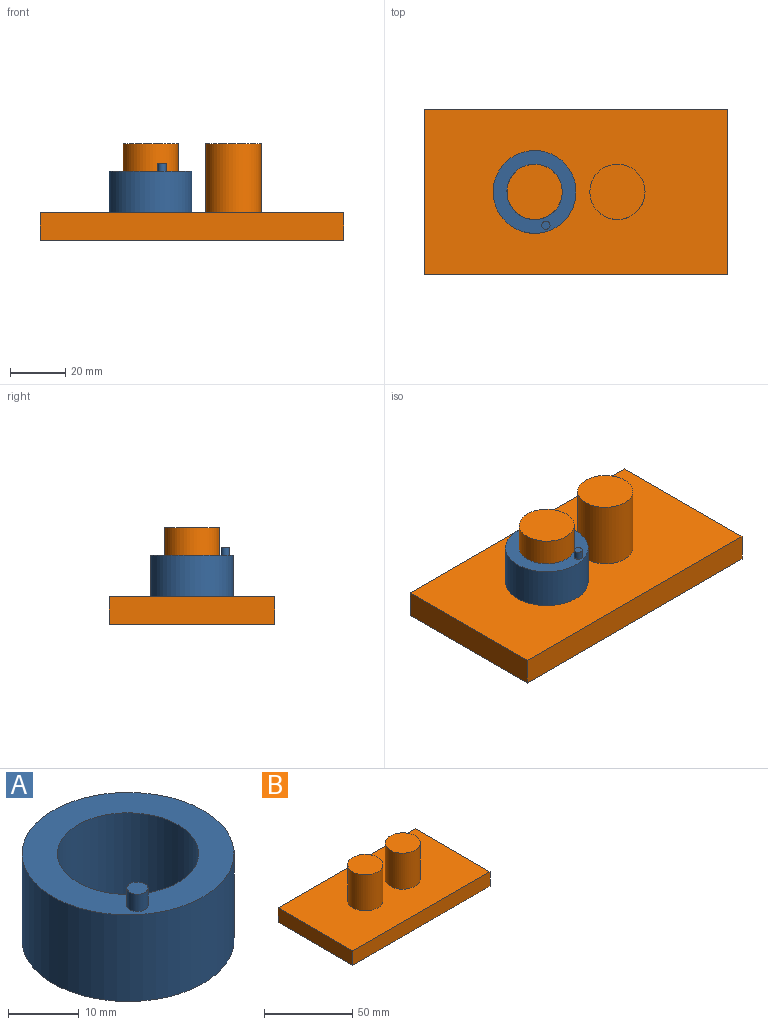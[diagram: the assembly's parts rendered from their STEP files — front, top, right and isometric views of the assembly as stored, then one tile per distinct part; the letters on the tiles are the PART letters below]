
ASSEMBLY  parts=2 mates=2
PART A: 6 faces, bbox 30x30x18 mm
  f0: cylinder r=10mm len=20mm, axis (0,0,-1), area 942.5mm2, adj f2,f3
  f1: cylinder r=15mm len=30mm, axis (0,0,-1), area 1413.7mm2, adj f2,f3
  f2: plane 30x30mm, normal (0,0,1), area 385.6mm2, adj f0,f1,f4
  f3: plane 30x30mm, normal (0,0,-1), area 392.7mm2, adj f0,f1
  f4: cylinder r=1.5mm len=3mm, axis (0,0,-1), area 28.3mm2, adj f2,f5
  f5: plane 3x3mm, normal (0,0,1), area 7.1mm2, adj f4
PART B: 10 faces, bbox 110x60x35 mm
  f0: plane 110x10mm, normal (0,1,0), area 1100mm2, adj f1,f3,f4,f5
  f1: plane 60x10mm, normal (-1,0,0), area 600mm2, adj f0,f2,f4,f5
  f2: plane 110x10mm, normal (0,-1,0), area 1100mm2, adj f1,f3,f4,f5
  f3: plane 60x10mm, normal (1,0,0), area 600mm2, adj f0,f2,f4,f5
  f4: plane 110x60mm, normal (0,0,1), area 5971.7mm2, adj f0,f1,f2,f3,f6,f8
  f5: plane 110x60mm, normal (0,0,-1), area 6600mm2, adj f0,f1,f2,f3
  f6: cylinder r=10mm len=25mm, axis (0,0,-1), area 1570.8mm2, adj f4,f7
  f7: plane 20x20mm, normal (0,0,1), area 314.2mm2, adj f6
  f8: cylinder r=10mm len=25mm, axis (0,0,-1), area 1570.8mm2, adj f4,f9
  f9: plane 20x20mm, normal (0,0,1), area 314.2mm2, adj f8
PLACE A rot(axis=(0,0,1),57.8deg) t=(14.54,31.47,-28.54)mm
PLACE B t=(-25.71,61.63,-38.54)mm fixed
MATE cylindrical A.f0 <-> B.f6  axis (0,0,-1) through (14.29,31.63,-21.04)mm
MATE planar A.f0 <-> B.f4  axis (0,0,-1) through (14.29,31.63,-28.54)mm
